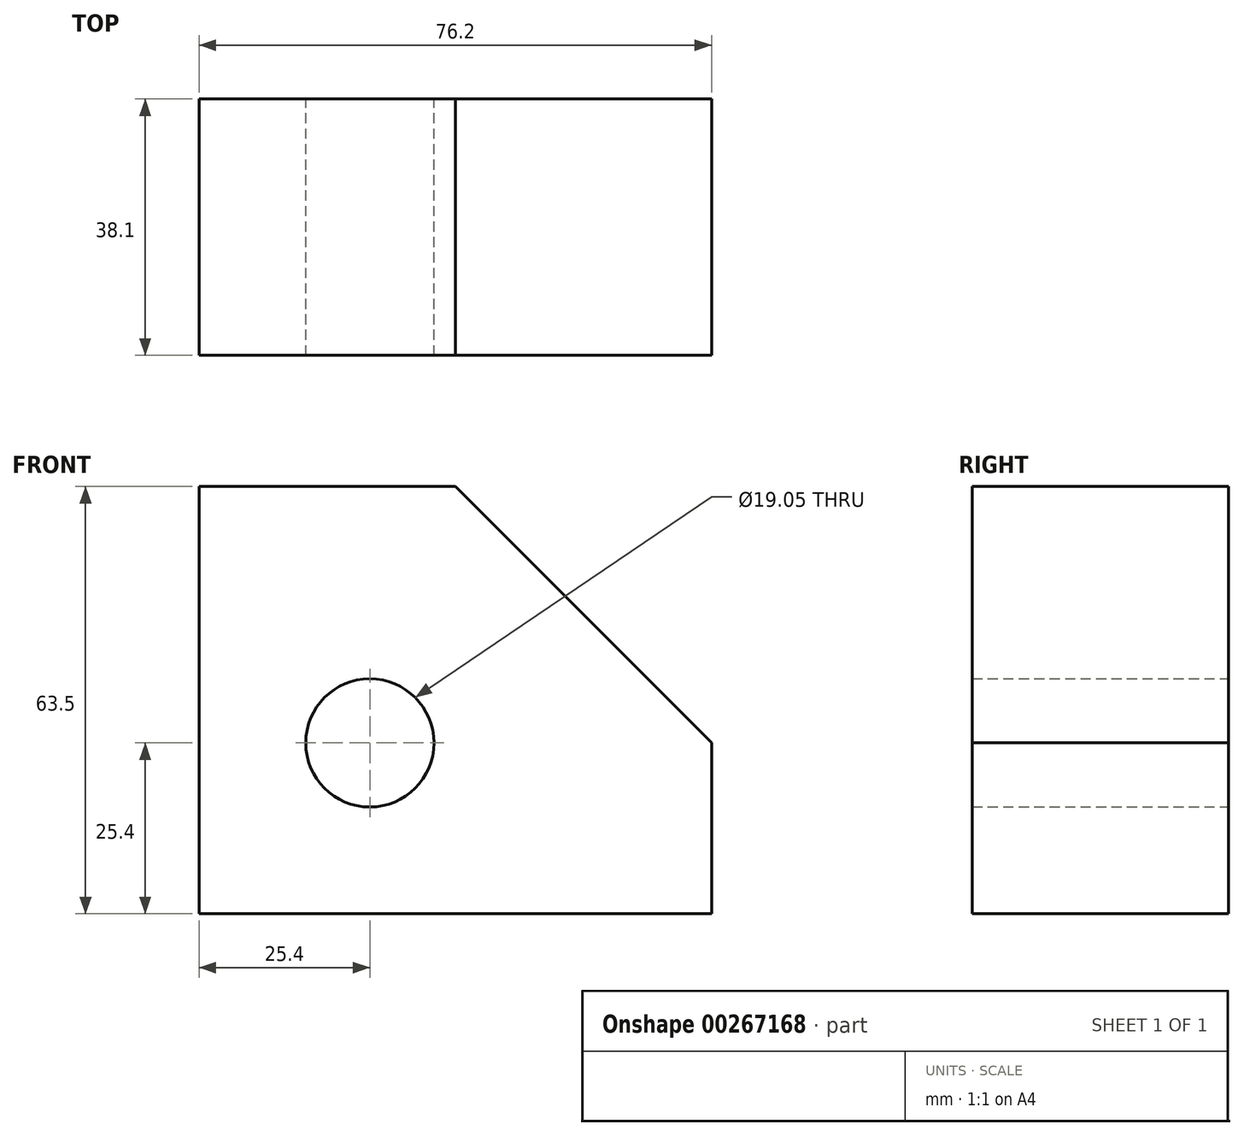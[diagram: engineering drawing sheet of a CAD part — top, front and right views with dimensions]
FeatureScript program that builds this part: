
annotation { "Feature Type Name" : "Feature", "Feature Type Description" : "" }
export const myFeature = defineFeature(function(context is Context, id is Id, definition is map)
    precondition{}
    {
        {
            var Q0;
            Q0=qCreatedBy(makeId("Front.planeOp"),FACE);
            var sketch = newSketch(context, id + "F0", { "sketchPlane" : qUnion([Q0])});
            skLineSegment(sketch, "E0", {"start": v(0, 0) * mm, "end": v(0, 63.5) * mm});
            skLineSegment(sketch, "E1", {"start": v(0, 63.5) * mm, "end": v(38.1, 63.5) * mm});
            skLineSegment(sketch, "E2", {"start": v(38.1, 63.5) * mm, "end": v(76.2, 25.4) * mm});
            skLineSegment(sketch, "E3", {"start": v(76.2, 25.4) * mm, "end": v(76.2, 0) * mm});
            skLineSegment(sketch, "E4", {"start": v(76.2, 0) * mm, "end": v(0, 0) * mm});
            skCircle(sketch, "E5", {"center": v(25.4, 25.4) * mm, "radius": 9.53 * mm});
            skSolve(sketch);
        }
        {
            var Q0;
            Q0 = qSketchRegion(id + "F0", true);
            extrude(context, id + "F1", {"entities" : qUnion([Q0]), "depth" : 38.1 * mm, "symmetric" : true});
        }
    });
